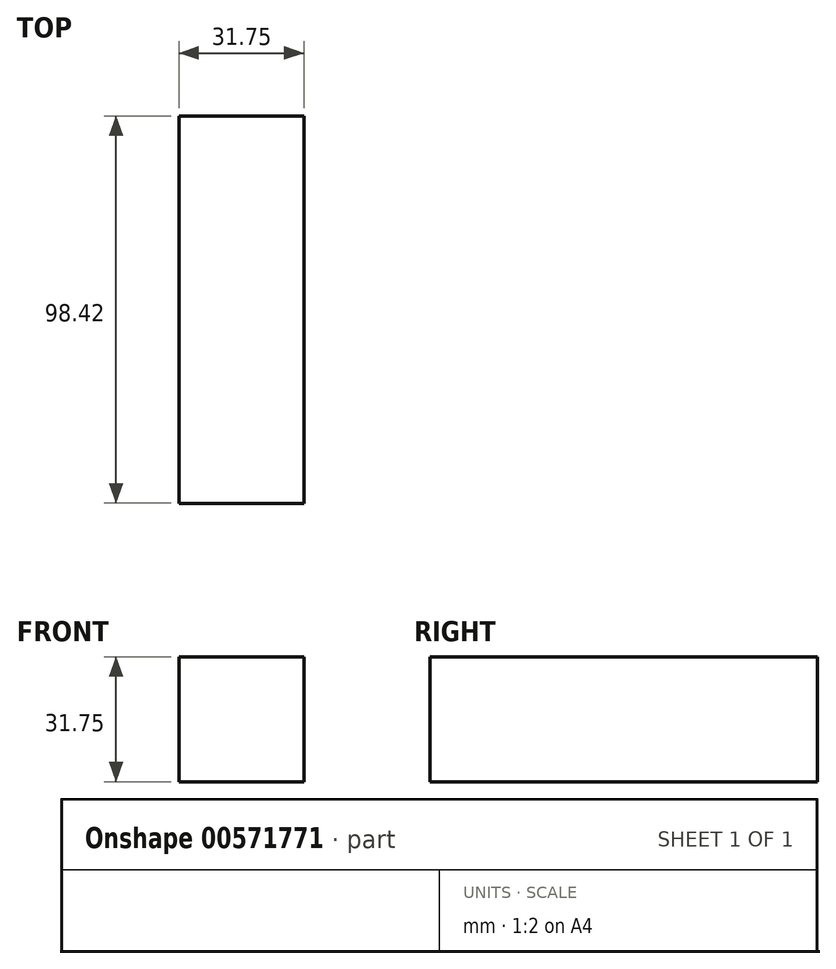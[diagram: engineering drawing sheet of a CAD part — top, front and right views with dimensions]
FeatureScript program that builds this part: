
annotation { "Feature Type Name" : "Feature", "Feature Type Description" : "" }
export const myFeature = defineFeature(function(context is Context, id is Id, definition is map)
    precondition{}
    {
        {
            var Q0;
            Q0=qCreatedBy(makeId("Front.planeOp"),FACE);
            var sketch = newSketch(context, id + "F0", { "sketchPlane" : qUnion([Q0])});
            skLineSegment(sketch, "E0.bottom", {"start": v(0, 0) * mm, "end": v(31.75, 0) * mm});
            skLineSegment(sketch, "E0.top", {"start": v(0, 31.75) * mm, "end": v(31.75, 31.75) * mm});
            skLineSegment(sketch, "E0.left", {"start": v(0, 0) * mm, "end": v(0, 31.75) * mm});
            skLineSegment(sketch, "E0.right", {"start": v(31.75, 0) * mm, "end": v(31.75, 31.75) * mm});
            skSolve(sketch);
        }
        {
            var Q0;
            Q0=makeQuery(id+"F0.imprint","IMPRINT",FACE,{"disambiguationData":[TD([[makeQuery(id+"F0.imprint","IMPRINT",EDGE,{"derivedFrom":sQuery(id+"F0.wireOp",EDGE,"E0.bottom")}),1.0]])]});
            extrude(context, id + "F1", {"entities" : qUnion([Q0]), "depth" : 98.42 * mm, "offsetDistance" : 25.4 * mm});
        }
    });
